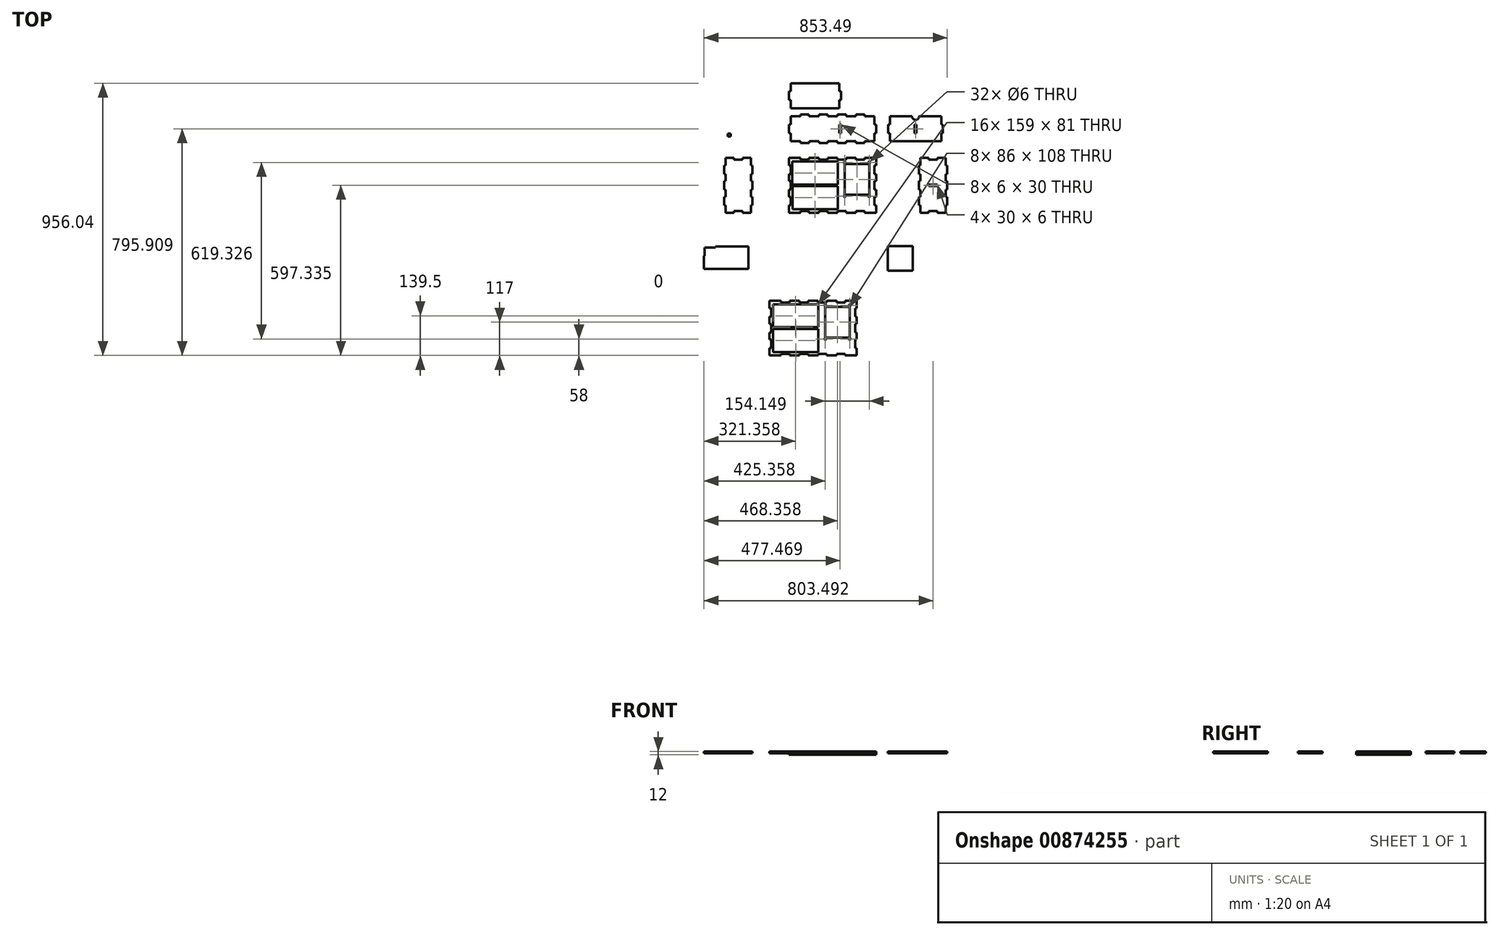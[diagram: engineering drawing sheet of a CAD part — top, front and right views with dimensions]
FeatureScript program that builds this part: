
annotation { "Feature Type Name" : "Feature", "Feature Type Description" : "" }
export const myFeature = defineFeature(function(context is Context, id is Id, definition is map)
    precondition{}
    {
        {
            var Q0;
            Q0=qCreatedBy(makeId("Top.planeOp"),FACE);
            var sketch = newSketch(context, id + "F0", { "sketchPlane" : qUnion([Q0])});
            skCircle(sketch, "E0", {"center": v(154.73, 68.9) * mm, "radius": 3 * mm});
            skCircle(sketch, "E1", {"center": v(154.73, -49.1) * mm, "radius": 3 * mm});
            skCircle(sketch, "E2", {"center": v(68.73, -49.1) * mm, "radius": 3 * mm});
            skCircle(sketch, "E3", {"center": v(68.73, 68.9) * mm, "radius": 3 * mm});
            skLineSegment(sketch, "E4.bottom", {"start": v(154.73, 63.9) * mm, "end": v(68.73, 63.9) * mm});
            skLineSegment(sketch, "E4.top", {"start": v(154.73, -44.1) * mm, "end": v(68.73, -44.1) * mm});
            skLineSegment(sketch, "E4.left", {"start": v(154.73, 63.9) * mm, "end": v(154.73, -44.1) * mm});
            skLineSegment(sketch, "E4.right", {"start": v(68.73, 63.9) * mm, "end": v(68.73, -44.1) * mm});
            skPoint(sketch, "E4.middle", {"position": v(111.73, 9.9) * mm});
            skLineSegment(sketch, "E5.bottom", {"start": v(44.23, -8.1) * mm, "end": v(-114.77, -8.1) * mm});
            skLineSegment(sketch, "E5.top", {"start": v(44.23, 72.9) * mm, "end": v(-114.77, 72.9) * mm});
            skLineSegment(sketch, "E5.left", {"start": v(44.23, -8.1) * mm, "end": v(44.23, 72.9) * mm});
            skLineSegment(sketch, "E5.right", {"start": v(-114.77, -8.1) * mm, "end": v(-114.77, 72.9) * mm});
            skLineSegment(sketch, "E6.MirrorCS", {"start": v(-114.55, -14.1) * mm, "end": v(-114.55, -95.1) * mm});
            skLineSegment(sketch, "E7.MirrorCS", {"start": v(44.45, -95.1) * mm, "end": v(-114.55, -95.1) * mm});
            skLineSegment(sketch, "E8.MirrorCS", {"start": v(44.45, -14.1) * mm, "end": v(-114.55, -14.1) * mm});
            skLineSegment(sketch, "E9.MirrorCS", {"start": v(44.45, -14.1) * mm, "end": v(44.45, -95.1) * mm});
            skLineSegment(sketch, "E10.bottom", {"start": v(-126.77, 84.9) * mm, "end": v(-86.27, 84.9) * mm});
            skLineSegment(sketch, "E10.top", {"start": v(-126.77, -107.1) * mm, "end": v(-86.27, -107.1) * mm});
            skLineSegment(sketch, "E10.left", {"start": v(-126.77, 84.9) * mm, "end": v(-126.77, 58.86) * mm});
            skLineSegment(sketch, "E10.right", {"start": v(179.23, 84.9) * mm, "end": v(179.23, 58.9) * mm});
            skLineSegment(sketch, "E11.0", {"start": v(42.23, 70.9) * mm, "end": v(-112.77, 70.9) * mm});
            skLineSegment(sketch, "E11.1", {"start": v(42.23, -6.1) * mm, "end": v(42.23, 70.9) * mm});
            skLineSegment(sketch, "E11.2", {"start": v(42.23, -6.1) * mm, "end": v(-112.77, -6.1) * mm});
            skLineSegment(sketch, "E11.3", {"start": v(-112.77, -6.1) * mm, "end": v(-112.77, 70.9) * mm});
            skLineSegment(sketch, "E12.0", {"start": v(-112.55, -16.1) * mm, "end": v(-112.55, -93.1) * mm});
            skLineSegment(sketch, "E12.1", {"start": v(42.45, -16.1) * mm, "end": v(-112.55, -16.1) * mm});
            skLineSegment(sketch, "E12.2", {"start": v(42.45, -16.1) * mm, "end": v(42.45, -93.1) * mm});
            skLineSegment(sketch, "E12.3", {"start": v(42.45, -93.1) * mm, "end": v(-112.55, -93.1) * mm});
            skLineSegment(sketch, "E13.bottom", {"start": v(179.23, 58.9) * mm, "end": v(173.23, 58.9) * mm});
            skLineSegment(sketch, "E13.top", {"start": v(179.23, 28.9) * mm, "end": v(173.23, 28.9) * mm});
            skLineSegment(sketch, "E13.right", {"start": v(173.23, 58.9) * mm, "end": v(173.23, 28.9) * mm});
            skLineSegment(sketch, "E14.top", {"start": v(-86.27, 78.9) * mm, "end": v(-56.27, 78.9) * mm});
            skLineSegment(sketch, "E14.left", {"start": v(-86.27, 84.9) * mm, "end": v(-86.27, 78.9) * mm});
            skLineSegment(sketch, "E14.right", {"start": v(-56.27, 84.9) * mm, "end": v(-56.27, 78.9) * mm});
            skLineSegment(sketch, "E15.top", {"start": v(-86.27, -101.1) * mm, "end": v(-56.27, -101.1) * mm});
            skLineSegment(sketch, "E15.left", {"start": v(-86.27, -107.1) * mm, "end": v(-86.27, -101.1) * mm});
            skLineSegment(sketch, "E15.right", {"start": v(-56.27, -107.1) * mm, "end": v(-56.27, -101.1) * mm});
            skLineSegment(sketch, "E16.trimOffspring", {"start": v(-56.27, 84.9) * mm, "end": v(-24.97, 84.9) * mm});
            skLineSegment(sketch, "E17.trimOffspring", {"start": v(-126.77, 19.9) * mm, "end": v(-126.77, 3.9) * mm});
            skLineSegment(sketch, "E18.trimOffspring", {"start": v(-126.77, -81.1) * mm, "end": v(-126.77, -107.1) * mm});
            skLineSegment(sketch, "E19.trimOffspring", {"start": v(-56.27, -107.1) * mm, "end": v(-21.27, -107.1) * mm});
            skLineSegment(sketch, "E20.trimOffspring", {"start": v(144.45, -107.1) * mm, "end": v(179.23, -107.1) * mm});
            skLineSegment(sketch, "E21.trimOffspring", {"start": v(179.23, -51.14) * mm, "end": v(179.23, -73.1) * mm});
            skLineSegment(sketch, "E22.trimOffspring", {"start": v(179.23, 28.9) * mm, "end": v(179.23, 3.9) * mm});
            skLineSegment(sketch, "E23.trimOffspring", {"start": v(138.5, 84.9) * mm, "end": v(179.23, 84.9) * mm});
            skLineSegment(sketch, "E24", {"start": v(114, 84.9) * mm, "end": v(114.1, 84.9) * mm});
            skLineSegment(sketch, "E25.trimOffspring", {"start": v(8.65, 84.9) * mm, "end": v(43.58, 84.9) * mm});
            skLineSegment(sketch, "E26.trimOffspring", {"start": v(73.58, 84.9) * mm, "end": v(114, 84.9) * mm});
            skLineSegment(sketch, "E27", {"start": v(-24.97, 84.9) * mm, "end": v(-21.35, 84.9) * mm});
            skLineSegment(sketch, "E28", {"start": v(43.58, 84.9) * mm, "end": v(47.52, 84.9) * mm});
            skLineSegment(sketch, "E29", {"start": v(108.5, 84.9) * mm, "end": v(114.1, 84.9) * mm});
            skLineSegment(sketch, "E30.1.0.0", {"start": v(-56.27, 84.9) * mm, "end": v(-21.35, 84.9) * mm});
            skLineSegment(sketch, "E30.1.0.1", {"start": v(-21.35, 78.9) * mm, "end": v(8.65, 78.9) * mm});
            skLineSegment(sketch, "E30.1.0.2", {"start": v(8.65, 84.9) * mm, "end": v(39.95, 84.9) * mm});
            skLineSegment(sketch, "E30.1.0.3", {"start": v(8.65, 84.9) * mm, "end": v(8.65, 78.9) * mm});
            skLineSegment(sketch, "E30.1.0.4", {"start": v(-21.35, 84.9) * mm, "end": v(-21.35, 78.9) * mm});
            skLineSegment(sketch, "E30.2.0.1", {"start": v(43.58, 78.9) * mm, "end": v(73.58, 78.9) * mm});
            skLineSegment(sketch, "E30.2.0.2", {"start": v(73.58, 84.9) * mm, "end": v(104.88, 84.9) * mm});
            skLineSegment(sketch, "E30.2.0.3", {"start": v(73.58, 84.9) * mm, "end": v(73.58, 78.9) * mm});
            skLineSegment(sketch, "E30.2.0.4", {"start": v(43.58, 84.9) * mm, "end": v(43.58, 78.9) * mm});
            skLineSegment(sketch, "E30.3.0.0", {"start": v(73.58, 84.9) * mm, "end": v(108.5, 84.9) * mm});
            skLineSegment(sketch, "E30.3.0.1", {"start": v(108.5, 78.9) * mm, "end": v(138.5, 78.9) * mm});
            skLineSegment(sketch, "E30.3.0.2", {"start": v(138.5, 84.9) * mm, "end": v(169.8, 84.9) * mm});
            skLineSegment(sketch, "E30.3.0.3", {"start": v(138.5, 84.9) * mm, "end": v(138.5, 78.9) * mm});
            skLineSegment(sketch, "E30.3.0.4", {"start": v(108.5, 84.9) * mm, "end": v(108.5, 78.9) * mm});
            skLineSegment(sketch, "E30.direction1", {"start": v(-126.77, 84.9) * mm, "end": v(-86.27, 84.9) * mm, "construction": true});
            skPoint(sketch, "E31.orphan", {"position": v(144.45, 84.9) * mm});
            skLineSegment(sketch, "E32", {"start": v(138.73, -107.1) * mm, "end": v(144.45, -107.1) * mm});
            skLineSegment(sketch, "E33.1.0.0", {"start": v(-21.27, -101.1) * mm, "end": v(8.73, -101.1) * mm});
            skLineSegment(sketch, "E33.1.0.1", {"start": v(-21.27, -107.1) * mm, "end": v(-21.27, -101.1) * mm});
            skLineSegment(sketch, "E33.1.0.2", {"start": v(8.73, -107.1) * mm, "end": v(8.73, -101.1) * mm});
            skLineSegment(sketch, "E33.2.0.0", {"start": v(43.73, -101.1) * mm, "end": v(73.73, -101.1) * mm});
            skLineSegment(sketch, "E33.2.0.1", {"start": v(43.73, -107.1) * mm, "end": v(43.73, -101.1) * mm});
            skLineSegment(sketch, "E33.2.0.2", {"start": v(73.73, -107.1) * mm, "end": v(73.73, -101.1) * mm});
            skLineSegment(sketch, "E33.3.0.0", {"start": v(108.73, -101.1) * mm, "end": v(138.73, -101.1) * mm});
            skLineSegment(sketch, "E33.3.0.1", {"start": v(108.73, -107.1) * mm, "end": v(108.73, -101.1) * mm});
            skLineSegment(sketch, "E33.3.0.2", {"start": v(138.73, -107.1) * mm, "end": v(138.73, -101.1) * mm});
            skLineSegment(sketch, "E33.direction1", {"start": v(-86.27, -107.1) * mm, "end": v(-21.27, -107.1) * mm, "construction": true});
            skPoint(sketch, "E34.orphan", {"position": v(-61.85, 84.9) * mm});
            skPoint(sketch, "E35.orphan", {"position": v(3.08, 84.9) * mm});
            skPoint(sketch, "E36.orphan", {"position": v(68, 84.9) * mm});
            skLineSegment(sketch, "E37.trimOffspring", {"start": v(8.73, -107.1) * mm, "end": v(43.73, -107.1) * mm});
            skLineSegment(sketch, "E38.trimOffspring", {"start": v(73.73, -107.1) * mm, "end": v(108.73, -107.1) * mm});
            skLineSegment(sketch, "E39", {"start": v(-126.77, -43.14) * mm, "end": v(-126.77, -51.1) * mm});
            skPoint(sketch, "E40.bottom.end.orphan", {"position": v(173.45, -72.1) * mm});
            skLineSegment(sketch, "E41", {"start": v(179.23, -43.14) * mm, "end": v(179.23, -51.14) * mm});
            skLineSegment(sketch, "E42.0.1.0", {"start": v(179.23, 3.9) * mm, "end": v(173.23, 3.9) * mm});
            skLineSegment(sketch, "E42.0.1.1", {"start": v(179.23, -26.1) * mm, "end": v(173.23, -26.1) * mm});
            skLineSegment(sketch, "E42.0.1.2", {"start": v(173.23, 3.9) * mm, "end": v(173.23, -26.1) * mm});
            skLineSegment(sketch, "E42.direction1", {"start": v(173.23, 28.9) * mm, "end": v(198.23, 28.9) * mm, "construction": true});
            skLineSegment(sketch, "E42.direction2", {"start": v(173.23, 28.9) * mm, "end": v(173.23, -26.1) * mm, "construction": true});
            skLineSegment(sketch, "E43.trimOffspring", {"start": v(179.23, -26.1) * mm, "end": v(179.23, -43.14) * mm});
            skLineSegment(sketch, "E44.trimOffspring", {"start": v(179.23, -81.07) * mm, "end": v(179.23, -107.1) * mm});
            skLineSegment(sketch, "E45", {"start": v(179.23, 84.9) * mm, "end": v(-126.77, -107.1) * mm, "construction": true});
            skLineSegment(sketch, "E46", {"start": v(-126.77, 84.9) * mm, "end": v(179.23, -107.1) * mm, "construction": true});
            skPoint(sketch, "E47", {"position": v(26.23, -11.1) * mm});
            skLineSegment(sketch, "E48", {"start": v(-126.77, 28.93) * mm, "end": v(-126.77, 19.9) * mm});
            skLineSegment(sketch, "E49.1.0", {"start": v(-126.77, -51.1) * mm, "end": v(-126.77, -26.1) * mm});
            skLineSegment(sketch, "E49.1.1", {"start": v(-120.77, 28.93) * mm, "end": v(-120.77, 58.86) * mm});
            skLineSegment(sketch, "E49.1.2", {"start": v(-120.77, -81.1) * mm, "end": v(-120.77, -51.1) * mm});
            skLineSegment(sketch, "E49.1.3", {"start": v(-120.77, -51.1) * mm, "end": v(-120.77, 3.9) * mm, "construction": true});
            skLineSegment(sketch, "E49.1.4", {"start": v(-126.77, 3.9) * mm, "end": v(-126.77, 20.93) * mm});
            skPoint(sketch, "E49.1.5", {"position": v(-121, 49.9) * mm});
            skLineSegment(sketch, "E49.1.6", {"start": v(-126.77, 58.86) * mm, "end": v(-126.77, 84.9) * mm});
            skLineSegment(sketch, "E49.1.8", {"start": v(-126.77, 20.93) * mm, "end": v(-126.77, 28.93) * mm});
            skLineSegment(sketch, "E49.1.9", {"start": v(-126.77, -107.1) * mm, "end": v(-126.77, -81.1) * mm});
            skLineSegment(sketch, "E49.1.10", {"start": v(-120.77, -51.1) * mm, "end": v(-145.77, -51.1) * mm, "construction": true});
            skLineSegment(sketch, "E49.1.11", {"start": v(-120.77, -26.1) * mm, "end": v(-120.77, 3.9) * mm});
            skLineSegment(sketch, "E49.1.12", {"start": v(-126.77, -51.1) * mm, "end": v(-120.77, -51.1) * mm});
            skLineSegment(sketch, "E49.1.13", {"start": v(-126.77, 28.93) * mm, "end": v(-120.77, 28.93) * mm});
            skLineSegment(sketch, "E49.1.14", {"start": v(-126.77, 58.86) * mm, "end": v(-120.77, 58.86) * mm});
            skLineSegment(sketch, "E49.1.15", {"start": v(-126.77, -81.1) * mm, "end": v(-120.77, -81.1) * mm});
            skLineSegment(sketch, "E49.1.16", {"start": v(-126.77, -26.1) * mm, "end": v(-120.77, -26.1) * mm});
            skLineSegment(sketch, "E49.1.17", {"start": v(-126.77, 3.9) * mm, "end": v(-120.77, 3.9) * mm});
            skLineSegment(sketch, "E50.trimOffspring", {"start": v(-126.77, -26.1) * mm, "end": v(-126.77, -43.14) * mm});
            skLineSegment(sketch, "E51.trimOffspring", {"start": v(-126.77, 50.9) * mm, "end": v(-126.77, 49.9) * mm});
            skLineSegment(sketch, "E52.trimOffspring", {"start": v(-126.77, 49.9) * mm, "end": v(-126.77, 50.9) * mm});
            skLineSegment(sketch, "E53.bottom", {"start": v(-260.55, 84.9) * mm, "end": v(-289.55, 84.9) * mm});
            skLineSegment(sketch, "E53.top", {"start": v(-260.55, -107.1) * mm, "end": v(-289.55, -107.1) * mm});
            skLineSegment(sketch, "E53.left", {"start": v(-260.55, 84.9) * mm, "end": v(-260.55, 58.86) * mm});
            skLineSegment(sketch, "E53.right", {"start": v(-348.55, 84.9) * mm, "end": v(-348.55, 58.9) * mm});
            skLineSegment(sketch, "E54.bottom", {"start": v(-260.55, 58.86) * mm, "end": v(-254.55, 58.86) * mm});
            skLineSegment(sketch, "E54.top", {"start": v(-260.55, 28.86) * mm, "end": v(-254.55, 28.86) * mm});
            skLineSegment(sketch, "E54.right", {"start": v(-254.55, 58.86) * mm, "end": v(-254.55, 28.86) * mm});
            skLineSegment(sketch, "E55.0.1.0", {"start": v(-260.55, 3.88) * mm, "end": v(-254.55, 3.88) * mm});
            skLineSegment(sketch, "E55.0.1.1", {"start": v(-260.55, -26.12) * mm, "end": v(-254.55, -26.12) * mm});
            skLineSegment(sketch, "E55.0.1.2", {"start": v(-254.55, 3.88) * mm, "end": v(-254.55, -26.12) * mm});
            skLineSegment(sketch, "E55.0.2.0", {"start": v(-260.55, -51.1) * mm, "end": v(-254.55, -51.1) * mm});
            skLineSegment(sketch, "E55.0.2.1", {"start": v(-260.55, -81.1) * mm, "end": v(-254.55, -81.1) * mm});
            skLineSegment(sketch, "E55.0.2.2", {"start": v(-254.55, -51.1) * mm, "end": v(-254.55, -81.1) * mm});
            skLineSegment(sketch, "E55.direction1", {"start": v(-260.55, 28.86) * mm, "end": v(-235.52, 28.86) * mm, "construction": true});
            skLineSegment(sketch, "E55.direction2", {"start": v(-260.55, 28.86) * mm, "end": v(-260.55, 3.88) * mm, "construction": true});
            skLineSegment(sketch, "E56.trimOffspring", {"start": v(-260.55, 28.86) * mm, "end": v(-260.55, 3.88) * mm});
            skLineSegment(sketch, "E57.trimOffspring", {"start": v(-260.55, -26.12) * mm, "end": v(-260.55, -51.1) * mm});
            skLineSegment(sketch, "E58.trimOffspring", {"start": v(-260.55, -81.1) * mm, "end": v(-260.55, -107.1) * mm});
            skLineSegment(sketch, "E59", {"start": v(-348.55, 84.9) * mm, "end": v(-260.55, -107.1) * mm, "construction": true});
            skLineSegment(sketch, "E60", {"start": v(-260.55, 84.9) * mm, "end": v(-348.55, -107.1) * mm, "construction": true});
            skPoint(sketch, "E61", {"position": v(-304.55, -11.1) * mm});
            skLineSegment(sketch, "E62.1.0", {"start": v(-348.55, -107.1) * mm, "end": v(-348.55, -81.07) * mm});
            skLineSegment(sketch, "E62.1.1", {"start": v(-348.55, -51.07) * mm, "end": v(-348.55, -26.09) * mm, "construction": true});
            skLineSegment(sketch, "E62.1.2", {"start": v(-354.55, 28.9) * mm, "end": v(-354.55, 58.9) * mm});
            skLineSegment(sketch, "E62.1.3", {"start": v(-354.55, -81.07) * mm, "end": v(-354.55, -51.07) * mm});
            skLineSegment(sketch, "E62.1.4", {"start": v(-348.55, 58.9) * mm, "end": v(-348.55, 84.9) * mm});
            skLineSegment(sketch, "E62.1.5", {"start": v(-354.55, -26.09) * mm, "end": v(-354.55, 3.91) * mm});
            skLineSegment(sketch, "E62.1.6", {"start": v(-348.55, -51.07) * mm, "end": v(-373.57, -51.07) * mm, "construction": true});
            skLineSegment(sketch, "E62.1.7", {"start": v(-348.55, 3.91) * mm, "end": v(-348.55, 28.9) * mm});
            skLineSegment(sketch, "E62.1.8", {"start": v(-348.55, -51.07) * mm, "end": v(-348.55, -26.09) * mm});
            skLineSegment(sketch, "E62.1.9", {"start": v(-348.55, 3.91) * mm, "end": v(-354.55, 3.91) * mm});
            skLineSegment(sketch, "E62.1.10", {"start": v(-348.55, -26.09) * mm, "end": v(-354.55, -26.09) * mm});
            skLineSegment(sketch, "E62.1.11", {"start": v(-348.55, 58.9) * mm, "end": v(-354.55, 58.9) * mm});
            skLineSegment(sketch, "E62.1.12", {"start": v(-348.55, 28.9) * mm, "end": v(-354.55, 28.9) * mm});
            skLineSegment(sketch, "E62.1.13", {"start": v(-348.55, -81.07) * mm, "end": v(-354.55, -81.07) * mm});
            skLineSegment(sketch, "E62.1.14", {"start": v(-348.55, -51.07) * mm, "end": v(-354.55, -51.07) * mm});
            skLineSegment(sketch, "E63.trimOffspring", {"start": v(-348.55, -26.09) * mm, "end": v(-348.55, -51.07) * mm});
            skLineSegment(sketch, "E64.trimOffspring", {"start": v(-348.55, -81.07) * mm, "end": v(-348.55, -107.1) * mm});
            skLineSegment(sketch, "E65.trimOffspring", {"start": v(-348.55, 28.9) * mm, "end": v(-348.55, 3.91) * mm});
            skLineSegment(sketch, "E66.top", {"start": v(-319.55, 78.9) * mm, "end": v(-289.55, 78.9) * mm});
            skLineSegment(sketch, "E66.left", {"start": v(-319.55, 84.9) * mm, "end": v(-319.55, 78.9) * mm});
            skLineSegment(sketch, "E66.right", {"start": v(-289.55, 84.9) * mm, "end": v(-289.55, 78.9) * mm});
            skLineSegment(sketch, "E67.trimOffspring", {"start": v(-319.55, 84.9) * mm, "end": v(-348.55, 84.9) * mm});
            skLineSegment(sketch, "E68.1.0", {"start": v(-289.55, -107.1) * mm, "end": v(-289.55, -101.1) * mm});
            skLineSegment(sketch, "E68.1.1", {"start": v(-319.55, -107.1) * mm, "end": v(-319.55, -101.1) * mm});
            skLineSegment(sketch, "E68.1.2", {"start": v(-289.55, -101.1) * mm, "end": v(-319.55, -101.1) * mm});
            skLineSegment(sketch, "E69.trimOffspring", {"start": v(-319.55, -107.1) * mm, "end": v(-348.55, -107.1) * mm});
            skLineSegment(sketch, "E70.bottom", {"start": v(-86.05, 137.48) * mm, "end": v(-56.05, 137.48) * mm});
            skLineSegment(sketch, "E70.top", {"start": v(-86.27, 237.48) * mm, "end": v(-56.27, 237.48) * mm});
            skLineSegment(sketch, "E70.left", {"start": v(-126.77, 172.48) * mm, "end": v(-126.77, 202.48) * mm});
            skLineSegment(sketch, "E70.right", {"start": v(179.23, 172.48) * mm, "end": v(179.23, 202.48) * mm});
            skLineSegment(sketch, "E71", {"start": v(-126.77, 137.48) * mm, "end": v(179.23, 84.9) * mm, "construction": true});
            skLineSegment(sketch, "E72", {"start": v(179.23, 137.48) * mm, "end": v(-126.77, 84.9) * mm, "construction": true});
            skPoint(sketch, "E73", {"position": v(26.23, 111.19) * mm});
            skLineSegment(sketch, "E74.1.13", {"start": v(8.88, 137.48) * mm, "end": v(8.88, 143.48) * mm});
            skLineSegment(sketch, "E74.1.14", {"start": v(43.8, 137.48) * mm, "end": v(43.8, 143.48) * mm});
            skLineSegment(sketch, "E74.1.15", {"start": v(-21.12, 137.48) * mm, "end": v(-21.12, 143.48) * mm});
            skLineSegment(sketch, "E74.1.17", {"start": v(-86.05, 137.48) * mm, "end": v(-86.05, 143.48) * mm});
            skLineSegment(sketch, "E74.1.18", {"start": v(73.8, 137.48) * mm, "end": v(73.8, 143.48) * mm});
            skLineSegment(sketch, "E74.1.19", {"start": v(-56.05, 137.48) * mm, "end": v(-56.05, 143.48) * mm});
            skLineSegment(sketch, "E74.1.20", {"start": v(138.73, 137.48) * mm, "end": v(138.73, 143.48) * mm});
            skLineSegment(sketch, "E74.1.21", {"start": v(108.73, 137.48) * mm, "end": v(108.73, 143.48) * mm});
            skLineSegment(sketch, "E74.1.22", {"start": v(-56.05, 137.48) * mm, "end": v(-61.55, 137.48) * mm});
            skLineSegment(sketch, "E74.1.23", {"start": v(-56.05, 137.48) * mm, "end": v(-61.65, 137.48) * mm});
            skLineSegment(sketch, "E74.1.25", {"start": v(8.88, 137.48) * mm, "end": v(4.93, 137.48) * mm});
            skLineSegment(sketch, "E74.1.26", {"start": v(-61.55, 137.48) * mm, "end": v(-61.65, 137.48) * mm});
            skLineSegment(sketch, "E75", {"start": v(-86.05, 143.48) * mm, "end": v(-120.77, 143.48) * mm});
            skLineSegment(sketch, "E76", {"start": v(-56.05, 143.48) * mm, "end": v(-21.12, 143.48) * mm});
            skLineSegment(sketch, "E77", {"start": v(8.88, 143.48) * mm, "end": v(43.8, 143.48) * mm});
            skLineSegment(sketch, "E78", {"start": v(73.8, 143.48) * mm, "end": v(108.73, 143.48) * mm});
            skLineSegment(sketch, "E79", {"start": v(138.73, 143.48) * mm, "end": v(173.23, 143.48) * mm});
            skLineSegment(sketch, "E80.trimOffspring", {"start": v(-21.12, 137.48) * mm, "end": v(8.88, 137.48) * mm});
            skLineSegment(sketch, "E81.trimOffspring", {"start": v(43.8, 137.48) * mm, "end": v(73.8, 137.48) * mm});
            skLineSegment(sketch, "E82.trimOffspring", {"start": v(108.73, 137.48) * mm, "end": v(138.73, 137.48) * mm});
            skLineSegment(sketch, "E83", {"start": v(-126.77, 237.48) * mm, "end": v(179.23, 137.48) * mm, "construction": true});
            skLineSegment(sketch, "E84", {"start": v(179.23, 237.48) * mm, "end": v(-126.77, 137.48) * mm, "construction": true});
            skPoint(sketch, "E85", {"position": v(26.23, 187.48) * mm});
            skLineSegment(sketch, "E86.1.0", {"start": v(-56.27, 237.48) * mm, "end": v(-86.27, 237.48) * mm});
            skLineSegment(sketch, "E86.1.1", {"start": v(138.5, 237.48) * mm, "end": v(108.5, 237.48) * mm});
            skLineSegment(sketch, "E86.1.2", {"start": v(8.65, 237.48) * mm, "end": v(-21.35, 237.48) * mm});
            skPoint(sketch, "E86.1.3", {"position": v(68.45, 230.3) * mm});
            skPoint(sketch, "E86.1.4", {"position": v(-61.55, 230.3) * mm});
            skLineSegment(sketch, "E86.1.5", {"start": v(73.58, 237.48) * mm, "end": v(43.58, 237.48) * mm});
            skLineSegment(sketch, "E86.1.6", {"start": v(-21.35, 231.48) * mm, "end": v(-56.27, 231.48) * mm});
            skLineSegment(sketch, "E86.1.7", {"start": v(43.58, 231.48) * mm, "end": v(8.65, 231.48) * mm});
            skPoint(sketch, "E86.1.8", {"position": v(3.45, 230.3) * mm});
            skLineSegment(sketch, "E86.1.9", {"start": v(108.5, 231.48) * mm, "end": v(73.58, 231.48) * mm});
            skLineSegment(sketch, "E86.1.10", {"start": v(43.58, 237.48) * mm, "end": v(43.58, 231.48) * mm});
            skLineSegment(sketch, "E86.1.11", {"start": v(-56.27, 237.48) * mm, "end": v(-56.27, 231.48) * mm});
            skLineSegment(sketch, "E86.1.12", {"start": v(-21.35, 237.48) * mm, "end": v(-21.35, 231.48) * mm});
            skLineSegment(sketch, "E86.1.13", {"start": v(-86.27, 237.48) * mm, "end": v(-86.27, 231.48) * mm});
            skLineSegment(sketch, "E86.1.14", {"start": v(108.5, 237.48) * mm, "end": v(108.5, 231.48) * mm});
            skLineSegment(sketch, "E86.1.15", {"start": v(138.5, 237.48) * mm, "end": v(138.5, 231.48) * mm});
            skLineSegment(sketch, "E86.1.16", {"start": v(8.65, 237.48) * mm, "end": v(8.65, 231.48) * mm});
            skLineSegment(sketch, "E86.1.17", {"start": v(73.58, 237.48) * mm, "end": v(73.58, 231.48) * mm});
            skLineSegment(sketch, "E86.1.18", {"start": v(43.58, 237.48) * mm, "end": v(47.52, 237.48) * mm});
            skLineSegment(sketch, "E86.1.19", {"start": v(108.5, 237.48) * mm, "end": v(114, 237.48) * mm});
            skLineSegment(sketch, "E86.1.20", {"start": v(108.5, 237.48) * mm, "end": v(114.1, 237.48) * mm});
            skLineSegment(sketch, "E86.1.21", {"start": v(114, 237.48) * mm, "end": v(114.1, 237.48) * mm});
            skLineSegment(sketch, "E87", {"start": v(-86.27, 231.48) * mm, "end": v(-120.77, 231.48) * mm});
            skLineSegment(sketch, "E88", {"start": v(138.5, 231.48) * mm, "end": v(173.23, 231.48) * mm});
            skLineSegment(sketch, "E89.trimOffspring", {"start": v(-21.35, 237.48) * mm, "end": v(8.65, 237.48) * mm});
            skLineSegment(sketch, "E90.trimOffspring", {"start": v(43.58, 237.48) * mm, "end": v(73.58, 237.48) * mm});
            skLineSegment(sketch, "E91.trimOffspring", {"start": v(108.5, 237.48) * mm, "end": v(138.5, 237.48) * mm});
            skLineSegment(sketch, "E92.left", {"start": v(-126.77, 187.48) * mm, "end": v(-126.77, 172.48) * mm});
            skLineSegment(sketch, "E93.bottom", {"start": v(-120.77, 202.48) * mm, "end": v(-126.77, 202.48) * mm});
            skLineSegment(sketch, "E93.top", {"start": v(-120.77, 172.48) * mm, "end": v(-126.77, 172.48) * mm});
            skLineSegment(sketch, "E93.left", {"start": v(-120.77, 202.48) * mm, "end": v(-120.77, 172.48) * mm});
            skPoint(sketch, "E93.middle", {"position": v(-126.77, 187.48) * mm});
            skLineSegment(sketch, "E94", {"start": v(-120.77, 202.48) * mm, "end": v(-120.77, 231.48) * mm});
            skLineSegment(sketch, "E95", {"start": v(-120.77, 172.48) * mm, "end": v(-120.77, 143.48) * mm});
            skPoint(sketch, "E96.1.0", {"position": v(179.23, 187.48) * mm});
            skLineSegment(sketch, "E96.1.1", {"start": v(179.23, 202.48) * mm, "end": v(179.23, 172.48) * mm});
            skLineSegment(sketch, "E96.1.2", {"start": v(179.23, 187.48) * mm, "end": v(179.23, 202.48) * mm});
            skLineSegment(sketch, "E96.1.3", {"start": v(173.23, 172.48) * mm, "end": v(173.23, 202.48) * mm});
            skLineSegment(sketch, "E96.1.4", {"start": v(173.23, 172.48) * mm, "end": v(179.23, 172.48) * mm});
            skLineSegment(sketch, "E96.1.5", {"start": v(173.23, 202.48) * mm, "end": v(179.23, 202.48) * mm});
            skLineSegment(sketch, "E97", {"start": v(173.23, 202.48) * mm, "end": v(173.23, 231.48) * mm});
            skLineSegment(sketch, "E98", {"start": v(173.23, 172.48) * mm, "end": v(173.23, 143.48) * mm});
            skLineSegment(sketch, "E99", {"start": v(43.58, 237.48) * mm, "end": v(73.8, 137.48) * mm, "construction": true});
            skLineSegment(sketch, "E100", {"start": v(73.58, 237.48) * mm, "end": v(43.8, 137.48) * mm, "construction": true});
            skPoint(sketch, "E101", {"position": v(58.69, 187.48) * mm});
            skLineSegment(sketch, "E102.right", {"start": v(55.69, 202.48) * mm, "end": v(55.69, 172.48) * mm});
            skLineSegment(sketch, "E103.MirrorCS", {"start": v(49.69, 172.48) * mm, "end": v(55.69, 172.48) * mm});
            skLineSegment(sketch, "E104.MirrorCS", {"start": v(49.69, 202.48) * mm, "end": v(55.69, 202.48) * mm});
            skLineSegment(sketch, "E105.MirrorCS", {"start": v(49.69, 202.48) * mm, "end": v(49.69, 172.48) * mm});
            skPoint(sketch, "E106.orphan", {"position": v(61.69, 202.48) * mm});
            skPoint(sketch, "E107.trimOffspring.end.orphan", {"position": v(61.69, 172.48) * mm});
            skLineSegment(sketch, "E108.bottom", {"start": v(227.4, 231.48) * mm, "end": v(304.9, 231.48) * mm});
            skLineSegment(sketch, "E108.top", {"start": v(227.4, 143.48) * mm, "end": v(407.4, 143.48) * mm});
            skLineSegment(sketch, "E108.left", {"start": v(227.4, 231.48) * mm, "end": v(227.4, 143.48) * mm});
            skLineSegment(sketch, "E108.right", {"start": v(407.4, 231.48) * mm, "end": v(407.4, 143.48) * mm});
            skLineSegment(sketch, "E109", {"start": v(173.23, 231.48) * mm, "end": v(227.4, 143.48) * mm, "construction": true});
            skLineSegment(sketch, "E110", {"start": v(227.4, 231.48) * mm, "end": v(173.23, 143.48) * mm, "construction": true});
            skPoint(sketch, "E111", {"position": v(200.32, 187.48) * mm});
            skPoint(sketch, "E112.1.0", {"position": v(221.4, 187.48) * mm});
            skLineSegment(sketch, "E112.1.1", {"start": v(227.4, 172.48) * mm, "end": v(221.4, 172.48) * mm});
            skLineSegment(sketch, "E112.1.2", {"start": v(221.4, 187.48) * mm, "end": v(221.4, 172.48) * mm});
            skLineSegment(sketch, "E112.1.3", {"start": v(227.4, 202.48) * mm, "end": v(221.4, 202.48) * mm});
            skLineSegment(sketch, "E112.1.4", {"start": v(221.4, 202.48) * mm, "end": v(221.4, 172.48) * mm});
            skLineSegment(sketch, "E112.1.5", {"start": v(227.4, 202.48) * mm, "end": v(227.4, 172.48) * mm});
            skLineSegment(sketch, "E112.1.6", {"start": v(221.4, 172.48) * mm, "end": v(221.4, 202.48) * mm});
            skLineSegment(sketch, "E113", {"start": v(227.4, 231.48) * mm, "end": v(407.4, 143.48) * mm, "construction": true});
            skLineSegment(sketch, "E114", {"start": v(407.4, 231.48) * mm, "end": v(227.4, 143.48) * mm, "construction": true});
            skLineSegment(sketch, "E115.1.0", {"start": v(413.4, 202.48) * mm, "end": v(413.4, 172.48) * mm});
            skPoint(sketch, "E115.1.1", {"position": v(413.4, 187.48) * mm});
            skLineSegment(sketch, "E115.1.2", {"start": v(407.4, 202.48) * mm, "end": v(413.4, 202.48) * mm});
            skLineSegment(sketch, "E115.1.3", {"start": v(407.4, 172.48) * mm, "end": v(413.4, 172.48) * mm});
            skLineSegment(sketch, "E115.1.4", {"start": v(407.4, 172.48) * mm, "end": v(407.4, 202.48) * mm});
            skLineSegment(sketch, "E115.1.5", {"start": v(413.4, 187.48) * mm, "end": v(413.4, 202.48) * mm});
            skLineSegment(sketch, "E115.1.6", {"start": v(413.4, 172.48) * mm, "end": v(413.4, 202.48) * mm});
            skPoint(sketch, "E115.center", {"position": v(317.4, 187.48) * mm});
            skLineSegment(sketch, "E116.bottom", {"start": v(320.4, 202.48) * mm, "end": v(314.4, 202.48) * mm});
            skLineSegment(sketch, "E116.top", {"start": v(320.4, 172.48) * mm, "end": v(314.4, 172.48) * mm});
            skLineSegment(sketch, "E116.left", {"start": v(320.4, 202.48) * mm, "end": v(320.4, 172.48) * mm});
            skLineSegment(sketch, "E116.right", {"start": v(314.4, 202.48) * mm, "end": v(314.4, 172.48) * mm});
            skLineSegment(sketch, "E117.1.0", {"start": v(179.23, -81.07) * mm, "end": v(173.23, -81.07) * mm});
            skLineSegment(sketch, "E117.1.1", {"start": v(173.23, -51.14) * mm, "end": v(173.23, -81.07) * mm});
            skLineSegment(sketch, "E117.1.2", {"start": v(179.23, -51.14) * mm, "end": v(173.23, -51.14) * mm});
            skLineSegment(sketch, "E118.bottom", {"start": v(422.71, 84.9) * mm, "end": v(393.71, 84.9) * mm});
            skLineSegment(sketch, "E118.top", {"start": v(422.71, -107.1) * mm, "end": v(393.71, -107.1) * mm});
            skLineSegment(sketch, "E118.left", {"start": v(422.71, 84.9) * mm, "end": v(422.71, 58.87) * mm});
            skLineSegment(sketch, "E118.right", {"start": v(334.71, 84.9) * mm, "end": v(334.71, 58.9) * mm});
            skLineSegment(sketch, "E119.bottom", {"start": v(422.71, 58.87) * mm, "end": v(428.71, 58.87) * mm});
            skLineSegment(sketch, "E119.top", {"start": v(422.71, 28.87) * mm, "end": v(428.71, 28.87) * mm});
            skLineSegment(sketch, "E119.right", {"start": v(428.71, 58.87) * mm, "end": v(428.71, 28.87) * mm});
            skLineSegment(sketch, "E120.0.1.0", {"start": v(422.71, 3.89) * mm, "end": v(428.71, 3.89) * mm});
            skLineSegment(sketch, "E120.0.1.1", {"start": v(422.71, -26.11) * mm, "end": v(428.71, -26.11) * mm});
            skLineSegment(sketch, "E120.0.1.2", {"start": v(428.71, 3.89) * mm, "end": v(428.71, -26.11) * mm});
            skLineSegment(sketch, "E120.0.2.0", {"start": v(422.71, -51.1) * mm, "end": v(428.71, -51.1) * mm});
            skLineSegment(sketch, "E120.0.2.1", {"start": v(422.71, -81.1) * mm, "end": v(428.71, -81.1) * mm});
            skLineSegment(sketch, "E120.0.2.2", {"start": v(428.71, -51.1) * mm, "end": v(428.71, -81.1) * mm});
            skLineSegment(sketch, "E120.direction2", {"start": v(422.71, 28.87) * mm, "end": v(422.71, 3.89) * mm, "construction": true});
            skLineSegment(sketch, "E121.trimOffspring", {"start": v(422.71, 28.87) * mm, "end": v(422.71, 3.89) * mm});
            skLineSegment(sketch, "E122.trimOffspring", {"start": v(422.71, -26.11) * mm, "end": v(422.71, -51.1) * mm});
            skLineSegment(sketch, "E123.trimOffspring", {"start": v(422.71, -81.1) * mm, "end": v(422.71, -107.1) * mm});
            skLineSegment(sketch, "E124", {"start": v(334.71, 84.9) * mm, "end": v(422.71, -107.1) * mm, "construction": true});
            skLineSegment(sketch, "E125", {"start": v(422.71, 84.9) * mm, "end": v(334.71, -107.1) * mm, "construction": true});
            skPoint(sketch, "E126", {"position": v(378.71, -11.1) * mm});
            skLineSegment(sketch, "E127.1.0", {"start": v(334.71, -107.1) * mm, "end": v(334.71, -81.06) * mm});
            skLineSegment(sketch, "E127.1.1", {"start": v(334.71, -51.06) * mm, "end": v(334.71, -26.08) * mm, "construction": true});
            skLineSegment(sketch, "E127.1.2", {"start": v(328.71, 28.9) * mm, "end": v(328.71, 58.9) * mm});
            skLineSegment(sketch, "E127.1.3", {"start": v(328.71, -81.06) * mm, "end": v(328.71, -51.06) * mm});
            skLineSegment(sketch, "E127.1.4", {"start": v(334.71, 58.9) * mm, "end": v(334.71, 84.9) * mm});
            skLineSegment(sketch, "E127.1.5", {"start": v(328.71, -26.08) * mm, "end": v(328.71, 3.92) * mm});
            skLineSegment(sketch, "E127.1.6", {"start": v(334.71, -51.06) * mm, "end": v(309.69, -51.06) * mm, "construction": true});
            skLineSegment(sketch, "E127.1.7", {"start": v(334.71, 3.92) * mm, "end": v(334.71, 28.9) * mm});
            skLineSegment(sketch, "E127.1.8", {"start": v(334.71, -51.06) * mm, "end": v(334.71, -26.08) * mm});
            skLineSegment(sketch, "E127.1.9", {"start": v(334.71, 3.92) * mm, "end": v(328.71, 3.92) * mm});
            skLineSegment(sketch, "E127.1.10", {"start": v(334.71, -26.08) * mm, "end": v(328.71, -26.08) * mm});
            skLineSegment(sketch, "E127.1.11", {"start": v(334.71, 58.9) * mm, "end": v(328.71, 58.9) * mm});
            skLineSegment(sketch, "E127.1.12", {"start": v(334.71, 28.9) * mm, "end": v(328.71, 28.9) * mm});
            skLineSegment(sketch, "E127.1.13", {"start": v(334.71, -81.06) * mm, "end": v(328.71, -81.06) * mm});
            skLineSegment(sketch, "E127.1.14", {"start": v(334.71, -51.06) * mm, "end": v(328.71, -51.06) * mm});
            skLineSegment(sketch, "E128.trimOffspring", {"start": v(334.71, -26.08) * mm, "end": v(334.71, -51.06) * mm});
            skLineSegment(sketch, "E129.trimOffspring", {"start": v(334.71, -81.06) * mm, "end": v(334.71, -107.1) * mm});
            skLineSegment(sketch, "E130.trimOffspring", {"start": v(334.71, 28.9) * mm, "end": v(334.71, 3.92) * mm});
            skLineSegment(sketch, "E131.top", {"start": v(363.71, 78.9) * mm, "end": v(393.71, 78.9) * mm});
            skLineSegment(sketch, "E131.left", {"start": v(363.71, 84.9) * mm, "end": v(363.71, 78.9) * mm});
            skLineSegment(sketch, "E131.right", {"start": v(393.71, 84.9) * mm, "end": v(393.71, 78.9) * mm});
            skLineSegment(sketch, "E132.trimOffspring", {"start": v(363.71, 84.9) * mm, "end": v(334.71, 84.9) * mm});
            skLineSegment(sketch, "E133.1.0", {"start": v(393.71, -107.1) * mm, "end": v(393.71, -101.1) * mm});
            skLineSegment(sketch, "E133.1.1", {"start": v(363.71, -107.1) * mm, "end": v(363.71, -101.1) * mm});
            skLineSegment(sketch, "E133.1.2", {"start": v(393.71, -101.1) * mm, "end": v(363.71, -101.1) * mm});
            skLineSegment(sketch, "E134.trimOffspring", {"start": v(363.71, -107.1) * mm, "end": v(334.71, -107.1) * mm});
            skLineSegment(sketch, "E135.bottom", {"start": v(393.71, -8.1) * mm, "end": v(363.71, -8.1) * mm});
            skLineSegment(sketch, "E135.top", {"start": v(393.71, -14.1) * mm, "end": v(363.71, -14.1) * mm});
            skLineSegment(sketch, "E135.left", {"start": v(393.71, -8.1) * mm, "end": v(393.71, -14.1) * mm});
            skLineSegment(sketch, "E135.right", {"start": v(363.71, -8.1) * mm, "end": v(363.71, -14.1) * mm});
            skLineSegment(sketch, "E136.bottom", {"start": v(-120.77, 259.61) * mm, "end": v(49.69, 259.61) * mm});
            skLineSegment(sketch, "E136.top", {"start": v(-120.77, 347.61) * mm, "end": v(49.69, 347.61) * mm});
            skLineSegment(sketch, "E136.left", {"start": v(-126.77, 288.61) * mm, "end": v(-126.77, 318.61) * mm});
            skLineSegment(sketch, "E136.right", {"start": v(55.69, 288.61) * mm, "end": v(55.69, 318.61) * mm});
            skLineSegment(sketch, "E137.bottom", {"start": v(-120.77, 318.61) * mm, "end": v(-126.77, 318.61) * mm});
            skLineSegment(sketch, "E137.top", {"start": v(-120.77, 288.61) * mm, "end": v(-126.77, 288.61) * mm});
            skPoint(sketch, "E137.middle", {"position": v(-126.77, 303.61) * mm});
            skLineSegment(sketch, "E138.bottom", {"start": v(55.69, 318.61) * mm, "end": v(49.69, 318.61) * mm});
            skLineSegment(sketch, "E138.top", {"start": v(55.69, 288.61) * mm, "end": v(49.69, 288.61) * mm});
            skPoint(sketch, "E138.middle", {"position": v(55.69, 303.61) * mm});
            skLineSegment(sketch, "E139", {"start": v(-120.77, 318.61) * mm, "end": v(-120.77, 347.61) * mm});
            skLineSegment(sketch, "E140", {"start": v(-120.77, 288.61) * mm, "end": v(-120.77, 259.61) * mm});
            skLineSegment(sketch, "E141", {"start": v(49.69, 318.61) * mm, "end": v(49.69, 347.61) * mm});
            skLineSegment(sketch, "E142", {"start": v(49.69, 288.61) * mm, "end": v(49.69, 259.61) * mm});
            skArc(sketch, "E143", {"start": v(304.9, 231.48) * mm, "mid": v(317.4, 218.98) * mm, "end": v(329.9, 231.48) * mm});
            skLineSegment(sketch, "E144.trimOffspring", {"start": v(329.9, 231.48) * mm, "end": v(407.4, 231.48) * mm});
            skLineSegment(sketch, "E145.bottom", {"start": v(-341.38, 170.05) * mm, "end": v(-331.38, 170.05) * mm});
            skLineSegment(sketch, "E145.top", {"start": v(-341.38, 160.05) * mm, "end": v(-331.38, 160.05) * mm});
            skLineSegment(sketch, "E145.left", {"start": v(-341.38, 170.05) * mm, "end": v(-341.38, 160.05) * mm});
            skLineSegment(sketch, "E145.right", {"start": v(-331.38, 170.05) * mm, "end": v(-331.38, 160.05) * mm});
            skCircle(sketch, "E146", {"center": v(86.58, -432.43) * mm, "radius": 3 * mm});
            skCircle(sketch, "E147", {"center": v(86.58, -550.43) * mm, "radius": 3 * mm});
            skCircle(sketch, "E148", {"center": v(0.58, -550.43) * mm, "radius": 3 * mm});
            skCircle(sketch, "E149", {"center": v(0.58, -432.43) * mm, "radius": 3 * mm});
            skLineSegment(sketch, "E150.bottom", {"start": v(86.58, -437.43) * mm, "end": v(0.58, -437.43) * mm});
            skLineSegment(sketch, "E150.top", {"start": v(86.58, -545.43) * mm, "end": v(0.58, -545.43) * mm});
            skLineSegment(sketch, "E150.left", {"start": v(86.58, -437.43) * mm, "end": v(86.58, -545.43) * mm});
            skLineSegment(sketch, "E150.right", {"start": v(0.58, -437.43) * mm, "end": v(0.58, -545.43) * mm});
            skPoint(sketch, "E150.middle", {"position": v(43.58, -491.43) * mm});
            skLineSegment(sketch, "E151.bottom", {"start": v(-23.92, -509.43) * mm, "end": v(-182.92, -509.43) * mm});
            skLineSegment(sketch, "E151.top", {"start": v(-23.92, -428.43) * mm, "end": v(-182.92, -428.43) * mm});
            skLineSegment(sketch, "E151.left", {"start": v(-23.92, -509.43) * mm, "end": v(-23.92, -428.43) * mm});
            skLineSegment(sketch, "E151.right", {"start": v(-182.92, -509.43) * mm, "end": v(-182.92, -428.43) * mm});
            skLineSegment(sketch, "E152.MirrorCS", {"start": v(-182.7, -515.43) * mm, "end": v(-182.7, -596.43) * mm});
            skLineSegment(sketch, "E153.MirrorCS", {"start": v(-23.7, -596.43) * mm, "end": v(-182.7, -596.43) * mm});
            skLineSegment(sketch, "E154.MirrorCS", {"start": v(-23.7, -515.43) * mm, "end": v(-182.7, -515.43) * mm});
            skLineSegment(sketch, "E155.MirrorCS", {"start": v(-23.7, -515.43) * mm, "end": v(-23.7, -596.43) * mm});
            skLineSegment(sketch, "E156.bottom", {"start": v(-194.92, -416.43) * mm, "end": v(-154.42, -416.43) * mm});
            skLineSegment(sketch, "E156.top", {"start": v(-194.92, -608.43) * mm, "end": v(-154.42, -608.43) * mm});
            skLineSegment(sketch, "E156.left", {"start": v(-194.92, -416.43) * mm, "end": v(-194.92, -442.46) * mm});
            skLineSegment(sketch, "E156.right", {"start": v(111.08, -416.43) * mm, "end": v(111.08, -442.43) * mm});
            skLineSegment(sketch, "E157.0", {"start": v(-25.92, -430.43) * mm, "end": v(-180.92, -430.43) * mm});
            skLineSegment(sketch, "E157.1", {"start": v(-25.92, -507.43) * mm, "end": v(-25.92, -430.43) * mm});
            skLineSegment(sketch, "E157.2", {"start": v(-25.92, -507.43) * mm, "end": v(-180.92, -507.43) * mm});
            skLineSegment(sketch, "E157.3", {"start": v(-180.92, -507.43) * mm, "end": v(-180.92, -430.43) * mm});
            skLineSegment(sketch, "E158.0", {"start": v(-180.7, -517.43) * mm, "end": v(-180.7, -594.43) * mm});
            skLineSegment(sketch, "E158.1", {"start": v(-25.7, -517.43) * mm, "end": v(-180.7, -517.43) * mm});
            skLineSegment(sketch, "E158.2", {"start": v(-25.7, -517.43) * mm, "end": v(-25.7, -594.43) * mm});
            skLineSegment(sketch, "E158.3", {"start": v(-25.7, -594.43) * mm, "end": v(-180.7, -594.43) * mm});
            skLineSegment(sketch, "E159.bottom", {"start": v(111.08, -442.43) * mm, "end": v(105.08, -442.43) * mm});
            skLineSegment(sketch, "E159.top", {"start": v(111.08, -472.43) * mm, "end": v(105.08, -472.43) * mm});
            skLineSegment(sketch, "E159.right", {"start": v(105.08, -442.43) * mm, "end": v(105.08, -472.43) * mm});
            skLineSegment(sketch, "E160.top", {"start": v(-154.42, -422.43) * mm, "end": v(-124.42, -422.43) * mm});
            skLineSegment(sketch, "E160.left", {"start": v(-154.42, -416.43) * mm, "end": v(-154.42, -422.43) * mm});
            skLineSegment(sketch, "E160.right", {"start": v(-124.42, -416.43) * mm, "end": v(-124.42, -422.43) * mm});
            skLineSegment(sketch, "E161.top", {"start": v(-154.42, -602.43) * mm, "end": v(-124.42, -602.43) * mm});
            skLineSegment(sketch, "E161.left", {"start": v(-154.42, -608.43) * mm, "end": v(-154.42, -602.43) * mm});
            skLineSegment(sketch, "E161.right", {"start": v(-124.42, -608.43) * mm, "end": v(-124.42, -602.43) * mm});
            skLineSegment(sketch, "E162.trimOffspring", {"start": v(-124.42, -416.43) * mm, "end": v(-93.12, -416.43) * mm});
            skLineSegment(sketch, "E163.trimOffspring", {"start": v(-194.92, -481.43) * mm, "end": v(-194.92, -497.43) * mm});
            skLineSegment(sketch, "E164.trimOffspring", {"start": v(-194.92, -582.43) * mm, "end": v(-194.92, -608.43) * mm});
            skLineSegment(sketch, "E165.trimOffspring", {"start": v(-124.42, -608.43) * mm, "end": v(-89.42, -608.43) * mm});
            skLineSegment(sketch, "E166.trimOffspring", {"start": v(76.3, -608.43) * mm, "end": v(111.08, -608.43) * mm});
            skLineSegment(sketch, "E167.trimOffspring", {"start": v(111.08, -552.46) * mm, "end": v(111.08, -574.43) * mm});
            skLineSegment(sketch, "E168.trimOffspring", {"start": v(111.08, -472.43) * mm, "end": v(111.08, -497.43) * mm});
            skLineSegment(sketch, "E169.trimOffspring", {"start": v(70.35, -416.43) * mm, "end": v(111.08, -416.43) * mm});
            skLineSegment(sketch, "E170", {"start": v(45.85, -416.43) * mm, "end": v(45.95, -416.43) * mm});
            skLineSegment(sketch, "E171.trimOffspring", {"start": v(-59.5, -416.43) * mm, "end": v(-24.57, -416.43) * mm});
            skLineSegment(sketch, "E172.trimOffspring", {"start": v(5.43, -416.43) * mm, "end": v(45.85, -416.43) * mm});
            skLineSegment(sketch, "E173", {"start": v(-93.12, -416.43) * mm, "end": v(-89.5, -416.43) * mm});
            skLineSegment(sketch, "E174", {"start": v(-24.57, -416.43) * mm, "end": v(-20.63, -416.43) * mm});
            skLineSegment(sketch, "E175", {"start": v(40.35, -416.43) * mm, "end": v(45.95, -416.43) * mm});
            skLineSegment(sketch, "E176.1.0.0", {"start": v(-124.42, -416.43) * mm, "end": v(-89.5, -416.43) * mm});
            skLineSegment(sketch, "E176.1.0.1", {"start": v(-89.5, -422.43) * mm, "end": v(-59.5, -422.43) * mm});
            skLineSegment(sketch, "E176.1.0.2", {"start": v(-59.5, -416.43) * mm, "end": v(-28.2, -416.43) * mm});
            skLineSegment(sketch, "E176.1.0.3", {"start": v(-59.5, -416.43) * mm, "end": v(-59.5, -422.43) * mm});
            skLineSegment(sketch, "E176.1.0.4", {"start": v(-89.5, -416.43) * mm, "end": v(-89.5, -422.43) * mm});
            skLineSegment(sketch, "E176.2.0.1", {"start": v(-24.57, -422.43) * mm, "end": v(5.43, -422.43) * mm});
            skLineSegment(sketch, "E176.2.0.2", {"start": v(5.43, -416.43) * mm, "end": v(36.73, -416.43) * mm});
            skLineSegment(sketch, "E176.2.0.3", {"start": v(5.43, -416.43) * mm, "end": v(5.43, -422.43) * mm});
            skLineSegment(sketch, "E176.2.0.4", {"start": v(-24.57, -416.43) * mm, "end": v(-24.57, -422.43) * mm});
            skLineSegment(sketch, "E176.3.0.0", {"start": v(5.43, -416.43) * mm, "end": v(40.35, -416.43) * mm});
            skLineSegment(sketch, "E176.3.0.1", {"start": v(40.35, -422.43) * mm, "end": v(70.35, -422.43) * mm});
            skLineSegment(sketch, "E176.3.0.2", {"start": v(70.35, -416.43) * mm, "end": v(101.65, -416.43) * mm});
            skLineSegment(sketch, "E176.3.0.3", {"start": v(70.35, -416.43) * mm, "end": v(70.35, -422.43) * mm});
            skLineSegment(sketch, "E176.3.0.4", {"start": v(40.35, -416.43) * mm, "end": v(40.35, -422.43) * mm});
            skLineSegment(sketch, "E176.direction1", {"start": v(-194.92, -416.43) * mm, "end": v(-154.42, -416.43) * mm, "construction": true});
            skPoint(sketch, "E177.orphan", {"position": v(76.3, -416.43) * mm});
            skLineSegment(sketch, "E178", {"start": v(70.58, -608.43) * mm, "end": v(76.3, -608.43) * mm});
            skLineSegment(sketch, "E179.1.0.0", {"start": v(-89.42, -602.43) * mm, "end": v(-59.42, -602.43) * mm});
            skLineSegment(sketch, "E179.1.0.1", {"start": v(-89.42, -608.43) * mm, "end": v(-89.42, -602.43) * mm});
            skLineSegment(sketch, "E179.1.0.2", {"start": v(-59.42, -608.43) * mm, "end": v(-59.42, -602.43) * mm});
            skLineSegment(sketch, "E179.2.0.0", {"start": v(-24.42, -602.43) * mm, "end": v(5.58, -602.43) * mm});
            skLineSegment(sketch, "E179.2.0.1", {"start": v(-24.42, -608.43) * mm, "end": v(-24.42, -602.43) * mm});
            skLineSegment(sketch, "E179.2.0.2", {"start": v(5.58, -608.43) * mm, "end": v(5.58, -602.43) * mm});
            skLineSegment(sketch, "E179.3.0.0", {"start": v(40.58, -602.43) * mm, "end": v(70.58, -602.43) * mm});
            skLineSegment(sketch, "E179.3.0.1", {"start": v(40.58, -608.43) * mm, "end": v(40.58, -602.43) * mm});
            skLineSegment(sketch, "E179.3.0.2", {"start": v(70.58, -608.43) * mm, "end": v(70.58, -602.43) * mm});
            skLineSegment(sketch, "E179.direction1", {"start": v(-154.42, -608.43) * mm, "end": v(-89.42, -608.43) * mm, "construction": true});
            skPoint(sketch, "E180.orphan", {"position": v(-130, -416.43) * mm});
            skPoint(sketch, "E181.orphan", {"position": v(-65.07, -416.43) * mm});
            skPoint(sketch, "E182.orphan", {"position": v(-0.15, -416.43) * mm});
            skLineSegment(sketch, "E183.trimOffspring", {"start": v(-59.42, -608.43) * mm, "end": v(-24.42, -608.43) * mm});
            skLineSegment(sketch, "E184.trimOffspring", {"start": v(5.58, -608.43) * mm, "end": v(40.58, -608.43) * mm});
            skLineSegment(sketch, "E185", {"start": v(-194.92, -544.46) * mm, "end": v(-194.92, -552.43) * mm});
            skPoint(sketch, "E186.bottom.end.orphan", {"position": v(105.3, -573.43) * mm});
            skLineSegment(sketch, "E187", {"start": v(111.08, -544.46) * mm, "end": v(111.08, -552.46) * mm});
            skLineSegment(sketch, "E188.0.1.0", {"start": v(111.08, -497.43) * mm, "end": v(105.08, -497.43) * mm});
            skLineSegment(sketch, "E188.0.1.1", {"start": v(111.08, -527.43) * mm, "end": v(105.08, -527.43) * mm});
            skLineSegment(sketch, "E188.0.1.2", {"start": v(105.08, -497.43) * mm, "end": v(105.08, -527.43) * mm});
            skLineSegment(sketch, "E188.direction1", {"start": v(105.08, -472.43) * mm, "end": v(130.08, -472.43) * mm, "construction": true});
            skLineSegment(sketch, "E188.direction2", {"start": v(105.08, -472.43) * mm, "end": v(105.08, -527.43) * mm, "construction": true});
            skLineSegment(sketch, "E189.trimOffspring", {"start": v(111.08, -527.43) * mm, "end": v(111.08, -544.46) * mm});
            skLineSegment(sketch, "E190.trimOffspring", {"start": v(111.08, -582.4) * mm, "end": v(111.08, -608.43) * mm});
            skLineSegment(sketch, "E191", {"start": v(111.08, -416.43) * mm, "end": v(-194.92, -608.43) * mm, "construction": true});
            skLineSegment(sketch, "E192", {"start": v(-194.92, -416.43) * mm, "end": v(111.08, -608.43) * mm, "construction": true});
            skPoint(sketch, "E193", {"position": v(-41.92, -512.43) * mm});
            skLineSegment(sketch, "E194", {"start": v(-194.92, -472.4) * mm, "end": v(-194.92, -481.43) * mm});
            skLineSegment(sketch, "E195.1.0", {"start": v(-194.92, -552.43) * mm, "end": v(-194.92, -527.43) * mm});
            skLineSegment(sketch, "E195.1.1", {"start": v(-188.92, -472.4) * mm, "end": v(-188.92, -442.46) * mm});
            skLineSegment(sketch, "E195.1.2", {"start": v(-188.92, -582.43) * mm, "end": v(-188.92, -552.43) * mm});
            skLineSegment(sketch, "E195.1.3", {"start": v(-188.92, -552.43) * mm, "end": v(-188.92, -497.43) * mm, "construction": true});
            skLineSegment(sketch, "E195.1.4", {"start": v(-194.92, -497.43) * mm, "end": v(-194.92, -480.4) * mm});
            skPoint(sketch, "E195.1.5", {"position": v(-189.15, -451.43) * mm});
            skLineSegment(sketch, "E195.1.6", {"start": v(-194.92, -442.46) * mm, "end": v(-194.92, -416.43) * mm});
            skLineSegment(sketch, "E195.1.8", {"start": v(-194.92, -480.4) * mm, "end": v(-194.92, -472.4) * mm});
            skLineSegment(sketch, "E195.1.9", {"start": v(-194.92, -608.43) * mm, "end": v(-194.92, -582.43) * mm});
            skLineSegment(sketch, "E195.1.10", {"start": v(-188.92, -552.43) * mm, "end": v(-213.92, -552.43) * mm, "construction": true});
            skLineSegment(sketch, "E195.1.11", {"start": v(-188.92, -527.43) * mm, "end": v(-188.92, -497.43) * mm});
            skLineSegment(sketch, "E195.1.12", {"start": v(-194.92, -552.43) * mm, "end": v(-188.92, -552.43) * mm});
            skLineSegment(sketch, "E195.1.13", {"start": v(-194.92, -472.4) * mm, "end": v(-188.92, -472.4) * mm});
            skLineSegment(sketch, "E195.1.14", {"start": v(-194.92, -442.46) * mm, "end": v(-188.92, -442.46) * mm});
            skLineSegment(sketch, "E195.1.15", {"start": v(-194.92, -582.43) * mm, "end": v(-188.92, -582.43) * mm});
            skLineSegment(sketch, "E195.1.16", {"start": v(-194.92, -527.43) * mm, "end": v(-188.92, -527.43) * mm});
            skLineSegment(sketch, "E195.1.17", {"start": v(-194.92, -497.43) * mm, "end": v(-188.92, -497.43) * mm});
            skLineSegment(sketch, "E196.trimOffspring", {"start": v(-194.92, -527.43) * mm, "end": v(-194.92, -544.46) * mm});
            skLineSegment(sketch, "E197.trimOffspring", {"start": v(-194.92, -450.43) * mm, "end": v(-194.92, -451.43) * mm});
            skLineSegment(sketch, "E198.trimOffspring", {"start": v(-194.92, -451.43) * mm, "end": v(-194.92, -450.43) * mm});
            skLineSegment(sketch, "E199.1.0", {"start": v(111.08, -582.4) * mm, "end": v(105.08, -582.4) * mm});
            skLineSegment(sketch, "E199.1.1", {"start": v(105.08, -552.46) * mm, "end": v(105.08, -582.4) * mm});
            skLineSegment(sketch, "E199.1.2", {"start": v(111.08, -552.46) * mm, "end": v(105.08, -552.46) * mm});
            skLineSegment(sketch, "E200.bottom", {"start": v(-268.78, -226.22) * mm, "end": v(-384.28, -226.22) * mm});
            skLineSegment(sketch, "E200.top", {"start": v(-268.78, -304.22) * mm, "end": v(-424.78, -304.22) * mm});
            skLineSegment(sketch, "E200.left", {"start": v(-268.78, -226.22) * mm, "end": v(-268.78, -304.22) * mm});
            skLineSegment(sketch, "E201.top", {"start": v(-424.78, -258.72) * mm, "end": v(-422.28, -258.72) * mm});
            skLineSegment(sketch, "E201.right", {"start": v(-422.28, -229.72) * mm, "end": v(-422.28, -258.72) * mm});
            skLineSegment(sketch, "E202.top", {"start": v(-422.28, -229.72) * mm, "end": v(-384.28, -229.72) * mm});
            skLineSegment(sketch, "E202.right", {"start": v(-384.28, -226.22) * mm, "end": v(-384.28, -229.72) * mm});
            skLineSegment(sketch, "E203.trimOffspring", {"start": v(-424.78, -258.72) * mm, "end": v(-424.78, -304.22) * mm});
            skLineSegment(sketch, "E204.bottom", {"start": v(219.97, -224.05) * mm, "end": v(307.97, -224.05) * mm});
            skLineSegment(sketch, "E204.top", {"start": v(219.97, -311.05) * mm, "end": v(307.97, -311.05) * mm});
            skLineSegment(sketch, "E204.left", {"start": v(219.97, -224.05) * mm, "end": v(219.97, -311.05) * mm});
            skLineSegment(sketch, "E204.right", {"start": v(307.97, -224.05) * mm, "end": v(307.97, -311.05) * mm});
            skSolve(sketch);
        }
        {
            var Q0;
            Q0 = qSketchRegion(id + "F0", true);
            extrude(context, id + "F1", {"entities" : qUnion([Q0]), "depth" : 6 * mm, "offsetDistance" : 25 * mm});
        }
        {
            var Q0;
            Q0=makeQuery(id+"F1.opExtrude","CAP_FACE",FACE,{"disambiguationData":[OSD([sQuery(id+"F0.wireOp",EDGE,"E0"),sQuery(id+"F0.wireOp",EDGE,"E1"),sQuery(id+"F0.wireOp",EDGE,"E2"),sQuery(id+"F0.wireOp",EDGE,"E3"),sQuery(id+"F0.wireOp",EDGE,"E4.bottom"),sQuery(id+"F0.wireOp",EDGE,"E4.top"),sQuery(id+"F0.wireOp",EDGE,"E4.left"),sQuery(id+"F0.wireOp",EDGE,"E4.right"),sQuery(id+"F0.wireOp",EDGE,"E5.bottom"),sQuery(id+"F0.wireOp",EDGE,"E5.top"),sQuery(id+"F0.wireOp",EDGE,"E5.left"),sQuery(id+"F0.wireOp",EDGE,"E5.right"),sQuery(id+"F0.wireOp",EDGE,"E6.MirrorCS"),sQuery(id+"F0.wireOp",EDGE,"E7.MirrorCS"),sQuery(id+"F0.wireOp",EDGE,"E8.MirrorCS"),sQuery(id+"F0.wireOp",EDGE,"E9.MirrorCS"),sQuery(id+"F0.wireOp",EDGE,"E10.bottom"),sQuery(id+"F0.wireOp",EDGE,"E10.top"),sQuery(id+"F0.wireOp",EDGE,"E10.left"),sQuery(id+"F0.wireOp",EDGE,"E10.right"),sQuery(id+"F0.wireOp",EDGE,"UHi5Y5kB-afGQ-uiFR-pG7i-S5mLV70GiCN8.bottom"),sQuery(id+"F0.wireOp",EDGE,"UHi5Y5kB-afGQ-uiFR-pG7i-S5mLV70GiCN8.top"),sQuery(id+"F0.wireOp",EDGE,"UHi5Y5kB-afGQ-uiFR-pG7i-S5mLV70GiCN8.right"),sQuery(id+"F0.wireOp",EDGE,"BTnL8ATx-RFrU-K6mu-ptFp-gTQ2TW2jcFMP.bottom"),sQuery(id+"F0.wireOp",EDGE,"BTnL8ATx-RFrU-K6mu-ptFp-gTQ2TW2jcFMP.top"),sQuery(id+"F0.wireOp",EDGE,"BTnL8ATx-RFrU-K6mu-ptFp-gTQ2TW2jcFMP.right"),sQuery(id+"F0.wireOp",EDGE,"E13.bottom"),sQuery(id+"F0.wireOp",EDGE,"E13.top"),sQuery(id+"F0.wireOp",EDGE,"E13.right"),sQuery(id+"F0.wireOp",EDGE,"E40.bottom"),sQuery(id+"F0.wireOp",EDGE,"E40.top"),sQuery(id+"F0.wireOp",EDGE,"E40.right"),sQuery(id+"F0.wireOp",EDGE,"E14.top"),sQuery(id+"F0.wireOp",EDGE,"E14.left"),sQuery(id+"F0.wireOp",EDGE,"E14.right"),sQuery(id+"F0.wireOp",EDGE,"mrVcvGJR-xtdt-vbac-uGd7-QKJhKXfsWntp.top"),sQuery(id+"F0.wireOp",EDGE,"mrVcvGJR-xtdt-vbac-uGd7-QKJhKXfsWntp.left"),sQuery(id+"F0.wireOp",EDGE,"mrVcvGJR-xtdt-vbac-uGd7-QKJhKXfsWntp.right"),sQuery(id+"F0.wireOp",EDGE,"E15.top"),sQuery(id+"F0.wireOp",EDGE,"E15.left"),sQuery(id+"F0.wireOp",EDGE,"E15.right"),sQuery(id+"F0.wireOp",EDGE,"ATMQMI35-RqwO-VZHg-8Kas-gkgAtmuvx5gX.top"),sQuery(id+"F0.wireOp",EDGE,"ATMQMI35-RqwO-VZHg-8Kas-gkgAtmuvx5gX.left"),sQuery(id+"F0.wireOp",EDGE,"ATMQMI35-RqwO-VZHg-8Kas-gkgAtmuvx5gX.right"),sQuery(id+"F0.wireOp",EDGE,"E16.trimOffspring"),sQuery(id+"F0.wireOp",EDGE,"E17.trimOffspring"),sQuery(id+"F0.wireOp",EDGE,"E18.trimOffspring"),sQuery(id+"F0.wireOp",EDGE,"E19.trimOffspring"),sQuery(id+"F0.wireOp",EDGE,"E20.trimOffspring"),sQuery(id+"F0.wireOp",EDGE,"E21.trimOffspring"),sQuery(id+"F0.wireOp",EDGE,"E22.trimOffspring"),sQuery(id+"F0.wireOp",EDGE,"E23.trimOffspring")])],"isStart":false});
            cPlane(context, id + "F2", {"entities" : qUnion([Q0]), "cplaneType" : CPlaneType.OFFSET, "offset" : 25 * mm, "width" : 150 * mm, "height" : 150 * mm});
        }
        {
            var Q0;
            Q0 = qSketchRegion(id + "F0", true);
            extrude(context, id + "F3", {"entities" : qUnion([Q0]), "depth" : 6 * mm, "offsetDistance" : 25 * mm});
        }
        {
            var Q0;
            Q0=qCreatedBy(makeId("Top.planeOp"),FACE);
            cPlane(context, id + "F4", {"entities" : qUnion([Q0]), "cplaneType" : CPlaneType.OFFSET, "offset" : 100 * mm, "oppositeDirection" : true, "width" : 150 * mm, "height" : 150 * mm});
        }
        {
            var Q0;
            Q0=makeQuery(id+"F0.imprint","IMPRINT",FACE,{"disambiguationData":[TD([[makeQuery(id+"F0.imprint","IMPRINT",EDGE,{"derivedFrom":sQuery(id+"F0.wireOp",EDGE,"E0")}),-1.0]])]});
            var Q1;
            Q1=makeQuery(id+"F0.imprint","IMPRINT",FACE,{"disambiguationData":[TD([[makeQuery(id+"F0.imprint","IMPRINT",EDGE,{"derivedFrom":sQuery(id+"F0.wireOp",EDGE,"E6.MirrorCS")}),1.0]])]});
            var Q2;
            Q2=makeQuery(id+"F0.imprint","IMPRINT",FACE,{"disambiguationData":[TD([[makeQuery(id+"F0.imprint","IMPRINT",EDGE,{"derivedFrom":sQuery(id+"F0.wireOp",EDGE,"E12.0")}),1.0]])]});
            var Q3;
            Q3=makeQuery(id+"F0.imprint","IMPRINT",FACE,{"disambiguationData":[TD([[makeQuery(id+"F0.imprint","IMPRINT",EDGE,{"derivedFrom":sQuery(id+"F0.wireOp",EDGE,"E5.bottom")}),-1.0]])]});
            var Q4;
            Q4=makeQuery(id+"F0.imprint","IMPRINT",FACE,{"disambiguationData":[TD([[makeQuery(id+"F0.imprint","IMPRINT",EDGE,{"derivedFrom":sQuery(id+"F0.wireOp",EDGE,"E11.0")}),1.0]])]});
            var Q5;
            Q5=makeQuery(id+"F0.imprint","IMPRINT",FACE,{"disambiguationData":[TD([[makeQuery(id+"F0.imprint","IMPRINT",EDGE,{"derivedFrom":sQuery(id+"F0.wireOp",EDGE,"E4.bottom")}),1.0]])]});
            var Q6;
            Q6=makeQuery(id+"F0.imprint","IMPRINT",FACE,{"disambiguationData":[TD([[makeQuery(id+"F0.imprint","IMPRINT",EDGE,{"derivedFrom":sQuery(id+"F0.wireOp",EDGE,"E3")}),1.0]])]});
            var Q7;
            Q7=makeQuery(id+"F0.imprint","IMPRINT",FACE,{"disambiguationData":[TD([[makeQuery(id+"F0.imprint","IMPRINT",EDGE,{"derivedFrom":sQuery(id+"F0.wireOp",EDGE,"E2")}),1.0]])]});
            var Q8;
            Q8=makeQuery(id+"F0.imprint","IMPRINT",FACE,{"disambiguationData":[TD([[makeQuery(id+"F0.imprint","IMPRINT",EDGE,{"derivedFrom":sQuery(id+"F0.wireOp",EDGE,"E1")}),1.0]])]});
            var Q9;
            Q9=makeQuery(id+"F0.imprint","IMPRINT",FACE,{"disambiguationData":[TD([[makeQuery(id+"F0.imprint","IMPRINT",EDGE,{"derivedFrom":sQuery(id+"F0.wireOp",EDGE,"E0")}),1.0]])]});
            var Q10;
            Q10=qCreatedBy(id+"F4.planeOp",FACE);
            extrude(context, id + "F5", {"entities" : qUnion([Q0, Q1, Q2, Q3, Q4, Q5, Q6, Q7, Q8, Q9]), "oppositeDirection" : true, "depth" : 6 * mm, "hasOffset" : true, "offsetDistance" : 25 * mm});
        }
    });
